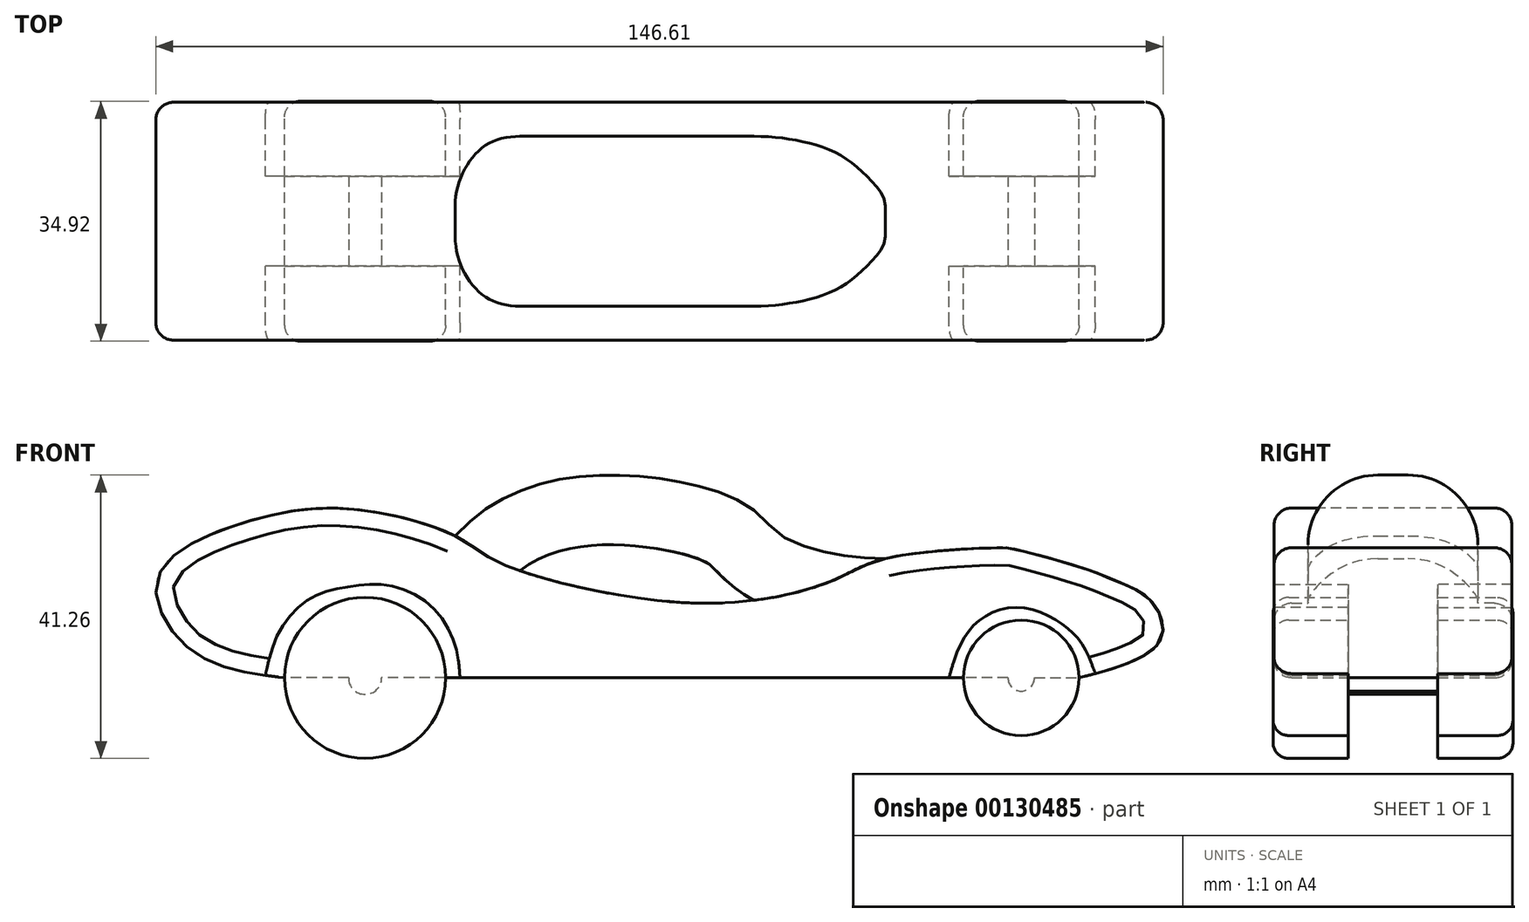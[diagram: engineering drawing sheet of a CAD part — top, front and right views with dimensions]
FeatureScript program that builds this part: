
annotation { "Feature Type Name" : "Feature", "Feature Type Description" : "" }
export const myFeature = defineFeature(function(context is Context, id is Id, definition is map)
    precondition{}
    {
        {
            var Q0;
            Q0=qCreatedBy(makeId("Front.planeOp"),FACE);
            var sketch = newSketch(context, id + "F0", { "sketchPlane" : qUnion([Q0])});
            skLineSegment(sketch, "E0", {"start": v(0, 0) * mm, "end": v(-51.5, 0) * mm});
            skLineSegment(sketch, "E1", {"start": v(0, 0) * mm, "end": v(34.83, 0) * mm});
            skCircle(sketch, "E2", {"center": v(-60.68, 0) * mm, "radius": 11.72 * mm});
            skCircle(sketch, "E3", {"center": v(34.83, 0) * mm, "radius": 8.41 * mm});
            skFitSpline(sketch, "E4", {"points": [v(-72.4, 0) * mm, v(-80.61, 1.45) * mm, v(-87.78, 5.65) * mm, v(-90.75, 14.91) * mm, v(-77.12, 22.96) * mm, v(-62.08, 24.53) * mm, v(-47.56, 20.68) * mm, v(-41.97, 17.19) * mm, v(-25, 12.29) * mm, v(-6.12, 11.07) * mm, v(7.52, 14.21) * mm, v(15.04, 17.36) * mm, v(31.47, 18.93) * mm, v(34.62, 18.59) * mm, v(45.46, 15.44) * mm, v(47.91, 14.39) * mm, v(53.5, 11.42) * mm, v(55.26, 5.82) * mm, v(50.36, 2.15) * mm, v(43.24, 0) * mm], "startDerivative": vector(-172.28, 21.35) * mm, "endDerivative": vector(-155.47, -39.98) * mm});
            skFitSpline(sketch, "E5", {"points": [v(-46.86, 0) * mm, v(-47.74, 5.3) * mm, v(-51.59, 10.9) * mm, v(-57.7, 13.51) * mm, v(-63.65, 13.16) * mm, v(-68.9, 11.42) * mm, v(-73.27, 6.52) * mm, v(-75.2, 0.35) * mm], "startDerivative": vector(-2.75, 39.39) * mm, "endDerivative": vector(-9.39, -43.26) * mm});
            skFitSpline(sketch, "E6", {"points": [v(24.3, 0) * mm, v(26.4, 5.65) * mm, v(29.9, 9.14) * mm, v(35.15, 10.2) * mm, v(40.4, 8.1) * mm, v(43.54, 5.12) * mm, v(45.62, 0.61) * mm], "startDerivative": vector(9.62, 33.45) * mm, "endDerivative": vector(11.2, -29.67) * mm});
            skFitSpline(sketch, "E7", {"points": [v(-47.56, 20.68) * mm, v(-42.14, 25.23) * mm, v(-31.3, 29.08) * mm, v(-15.91, 28.73) * mm, v(-4.72, 24.88) * mm, v(0, 20.68) * mm, v(8.57, 17.89) * mm, v(15.04, 17.36) * mm], "startDerivative": vector(38.88, 38.37) * mm, "endDerivative": vector(50.96, -1.8) * mm});
            skCircle(sketch, "E8", {"center": v(-60.68, 0) * mm, "radius": 2.4 * mm});
            skCircle(sketch, "E9", {"center": v(34.83, 0) * mm, "radius": 1.93 * mm});
            skCircle(sketch, "E10", {"center": v(-60.68, 0) * mm, "radius": 9.22 * mm});
            skCircle(sketch, "E11", {"center": v(34.83, 0) * mm, "radius": 6.25 * mm});
            skLineSegment(sketch, "E12", {"start": v(34.83, 0) * mm, "end": v(43.24, 0) * mm});
            skLineSegment(sketch, "E13", {"start": v(-51.5, 0) * mm, "end": v(-72.4, 0) * mm});
            skArc(sketch, "E14", {"start": v(-73.25, 0.1) * mm, "mid": v(-60.54, -12.95) * mm, "end": v(-47.72, 0) * mm});
            skArc(sketch, "E15", {"start": v(25.75, 0) * mm, "mid": v(34.96, -9.02) * mm, "end": v(43.99, 0.2) * mm});
            skSolve(sketch);
        }
        {
            var Q0;
            {var subQ6=sQuery(id+"F0.wireOp",EDGE,"E1");var subQ7=sQuery(id+"F0.wireOp",EDGE,"E0");var subQ8=makeQuery(id+"F0.imprint","INTERSECT",VERTEX,{"derivedFrom":[subQ7,subQ6]});Q0=makeQuery(id+"F0.imprint","IMPRINT",FACE,{"disambiguationData":[TD([[makeQuery(id+"F0.imprint","IMPRINT",EDGE,{"disambiguationData":[TD([[subQ8,-1.0]])],"derivedFrom":subQ7}),-1.0]])]});}
            extrude(context, id + "F1", {"entities" : qUnion([Q0]), "endBound" : BoundingType.SYMMETRIC, "depth" : 34.63 * mm});
        }
        {
            var Q0;
            {var subQ0=sQuery(id+"F0.wireOp",EDGE,"E7");Q0=makeQuery(id+"F0.imprint","IMPRINT",FACE,{"disambiguationData":[TD([[makeQuery(id+"F0.imprint","IMPRINT",EDGE,{"derivedFrom":subQ0}),-1.0]])]});}
            extrude(context, id + "F2", {"entities" : qUnion([Q0]), "operationType" : NewBodyOperationType.ADD, "endBound" : BoundingType.SYMMETRIC, "depth" : 24.74 * mm});
        }
        {
            var Q0;
            {var subQ0=sQuery(id+"F0.wireOp",EDGE,"E3");var subQ1=sQuery(id+"F0.wireOp",EDGE,"E1");var subQ2=makeQuery(id+"F0.imprint","INTERSECT",VERTEX,{"derivedFrom":[subQ1,subQ0]});Q0=makeQuery(id+"F0.imprint","IMPRINT",FACE,{"disambiguationData":[TD([[makeQuery(id+"F0.imprint","IMPRINT",EDGE,{"disambiguationData":[TD([[subQ2,-1.0]])],"derivedFrom":subQ1}),-1.0]])]});}
            var Q1;
            {var subQ0=sQuery(id+"F0.wireOp",EDGE,"E11");var subQ1=sQuery(id+"F0.wireOp",EDGE,"E1");var subQ2=makeQuery(id+"F0.imprint","INTERSECT",VERTEX,{"derivedFrom":[subQ1,subQ0]});Q1=makeQuery(id+"F0.imprint","IMPRINT",FACE,{"disambiguationData":[TD([[makeQuery(id+"F0.imprint","IMPRINT",EDGE,{"disambiguationData":[TD([[subQ2,-1.0]])],"derivedFrom":subQ1}),-1.0]])]});}
            var Q2;
            {var subQ0=sQuery(id+"F0.wireOp",EDGE,"E12");var subQ1=sQuery(id+"F0.wireOp",EDGE,"E1");var subQ2=makeQuery(id+"F0.imprint","INTERSECT",VERTEX,{"derivedFrom":[subQ1,subQ0]});Q2=makeQuery(id+"F0.imprint","IMPRINT",FACE,{"disambiguationData":[TD([[makeQuery(id+"F0.imprint","IMPRINT",EDGE,{"disambiguationData":[TD([[subQ2,1.0]])],"derivedFrom":subQ1}),-1.0]])]});}
            var Q3;
            {var subQ0=sQuery(id+"F0.wireOp",EDGE,"E11");var subQ1=sQuery(id+"F0.wireOp",EDGE,"E1");var subQ2=makeQuery(id+"F0.imprint","INTERSECT",VERTEX,{"derivedFrom":[subQ1,subQ0]});Q3=makeQuery(id+"F0.imprint","IMPRINT",FACE,{"disambiguationData":[TD([[makeQuery(id+"F0.imprint","IMPRINT",EDGE,{"disambiguationData":[TD([[subQ2,-1.0]])],"derivedFrom":subQ1}),1.0]])]});}
            var Q4;
            {var subQ0=sQuery(id+"F0.wireOp",EDGE,"E12");var subQ1=sQuery(id+"F0.wireOp",EDGE,"E1");var subQ2=makeQuery(id+"F0.imprint","INTERSECT",VERTEX,{"derivedFrom":[subQ1,subQ0]});Q4=makeQuery(id+"F0.imprint","IMPRINT",FACE,{"disambiguationData":[TD([[makeQuery(id+"F0.imprint","IMPRINT",EDGE,{"disambiguationData":[TD([[subQ2,1.0]])],"derivedFrom":subQ1}),1.0]])]});}
            var Q5;
            {var subQ0=sQuery(id+"F0.wireOp",EDGE,"E3");var subQ1=sQuery(id+"F0.wireOp",EDGE,"E1");var subQ2=makeQuery(id+"F0.imprint","INTERSECT",VERTEX,{"derivedFrom":[subQ1,subQ0]});Q5=makeQuery(id+"F0.imprint","IMPRINT",FACE,{"disambiguationData":[TD([[makeQuery(id+"F0.imprint","IMPRINT",EDGE,{"disambiguationData":[TD([[subQ2,-1.0]])],"derivedFrom":subQ1}),1.0]])]});}
            var Q6;
            {var subQ0=sQuery(id+"F0.wireOp",EDGE,"E2");var subQ1=sQuery(id+"F0.wireOp",EDGE,"E0");var subQ2=makeQuery(id+"F0.imprint","INTERSECT",VERTEX,{"derivedFrom":[subQ1,subQ0]});Q6=makeQuery(id+"F0.imprint","IMPRINT",FACE,{"disambiguationData":[TD([[makeQuery(id+"F0.imprint","IMPRINT",EDGE,{"disambiguationData":[TD([[subQ2,-1.0]])],"derivedFrom":subQ1}),-1.0]])]});}
            var Q7;
            {var subQ1=sQuery(id+"F0.wireOp",EDGE,"E0");var subQ3=sQuery(id+"F0.wireOp",EDGE,"E13");var subQ8=makeQuery(id+"F0.imprint","INTERSECT",VERTEX,{"derivedFrom":[subQ1,subQ3]});Q7=makeQuery(id+"F0.imprint","IMPRINT",FACE,{"disambiguationData":[TD([[makeQuery(id+"F0.imprint","IMPRINT",EDGE,{"disambiguationData":[TD([[subQ8,1.0]])],"derivedFrom":subQ1}),-1.0]])]});}
            var Q8;
            {var subQ1=sQuery(id+"F0.wireOp",EDGE,"E0");var subQ3=sQuery(id+"F0.wireOp",EDGE,"E13");var subQ8=makeQuery(id+"F0.imprint","INTERSECT",VERTEX,{"derivedFrom":[subQ1,subQ3]});Q8=makeQuery(id+"F0.imprint","IMPRINT",FACE,{"disambiguationData":[TD([[makeQuery(id+"F0.imprint","IMPRINT",EDGE,{"disambiguationData":[TD([[subQ8,1.0]])],"derivedFrom":subQ1}),1.0]])]});}
            var Q9;
            {var subQ0=sQuery(id+"F0.wireOp",EDGE,"E2");var subQ1=sQuery(id+"F0.wireOp",EDGE,"E0");var subQ2=makeQuery(id+"F0.imprint","INTERSECT",VERTEX,{"derivedFrom":[subQ1,subQ0]});Q9=makeQuery(id+"F0.imprint","IMPRINT",FACE,{"disambiguationData":[TD([[makeQuery(id+"F0.imprint","IMPRINT",EDGE,{"disambiguationData":[TD([[subQ2,-1.0]])],"derivedFrom":subQ1}),1.0]])]});}
            var Q10;
            {var subQ0=sQuery(id+"F0.wireOp",EDGE,"E13");var subQ1=sQuery(id+"F0.wireOp",EDGE,"E8");var subQ2=makeQuery(id+"F0.imprint","INTERSECT",VERTEX,{"disambiguationData":[OD(0.0)],"derivedFrom":[subQ1,subQ0]});Q10=makeQuery(id+"F0.imprint","IMPRINT",FACE,{"disambiguationData":[TD([[makeQuery(id+"F0.imprint","IMPRINT",EDGE,{"disambiguationData":[TD([[subQ2,1.0]])],"derivedFrom":subQ1}),1.0]])]});}
            var Q11;
            {var subQ0=sQuery(id+"F0.wireOp",EDGE,"E13");var subQ1=sQuery(id+"F0.wireOp",EDGE,"E8");var subQ2=makeQuery(id+"F0.imprint","INTERSECT",VERTEX,{"disambiguationData":[OD(0.0)],"derivedFrom":[subQ1,subQ0]});Q11=makeQuery(id+"F0.imprint","IMPRINT",FACE,{"disambiguationData":[TD([[makeQuery(id+"F0.imprint","IMPRINT",EDGE,{"disambiguationData":[TD([[subQ2,-1.0]])],"derivedFrom":subQ1}),1.0]])]});}
            extrude(context, id + "F3", {"entities" : qUnion([Q0, Q1, Q2, Q3, Q4, Q5, Q6, Q7, Q8, Q9, Q10, Q11]), "endBound" : BoundingType.SYMMETRIC, "depth" : 34.92 * mm});
        }
        {
            var Q0;
            {var subQ0=sQuery(id+"F0.wireOp",EDGE,"E5");var subQ1=sQuery(id+"F0.wireOp",EDGE,"E0");var subQ2=makeQuery(id+"F0.imprint","INTERSECT",VERTEX,{"derivedFrom":[subQ1,subQ0]});Q0=makeQuery(id+"F0.imprint","IMPRINT",FACE,{"disambiguationData":[TD([[makeQuery(id+"F0.imprint","IMPRINT",EDGE,{"disambiguationData":[TD([[subQ2,-1.0]])],"derivedFrom":subQ1}),-1.0]])]});}
            var Q1;
            {var subQ1=sQuery(id+"F0.wireOp",EDGE,"E0");var subQ3=sQuery(id+"F0.wireOp",EDGE,"E13");var subQ8=makeQuery(id+"F0.imprint","INTERSECT",VERTEX,{"derivedFrom":[subQ1,subQ3]});Q1=makeQuery(id+"F0.imprint","IMPRINT",FACE,{"disambiguationData":[TD([[makeQuery(id+"F0.imprint","IMPRINT",EDGE,{"disambiguationData":[TD([[subQ8,1.0]])],"derivedFrom":subQ1}),-1.0]])]});}
            var Q2;
            {var subQ0=sQuery(id+"F0.wireOp",EDGE,"E2");var subQ1=sQuery(id+"F0.wireOp",EDGE,"E0");var subQ2=makeQuery(id+"F0.imprint","INTERSECT",VERTEX,{"derivedFrom":[subQ1,subQ0]});Q2=makeQuery(id+"F0.imprint","IMPRINT",FACE,{"disambiguationData":[TD([[makeQuery(id+"F0.imprint","IMPRINT",EDGE,{"disambiguationData":[TD([[subQ2,-1.0]])],"derivedFrom":subQ1}),-1.0]])]});}
            var Q3;
            {var subQ0=sQuery(id+"F0.wireOp",EDGE,"E13");var subQ1=sQuery(id+"F0.wireOp",EDGE,"E8");var subQ2=makeQuery(id+"F0.imprint","INTERSECT",VERTEX,{"disambiguationData":[OD(0.0)],"derivedFrom":[subQ1,subQ0]});Q3=makeQuery(id+"F0.imprint","IMPRINT",FACE,{"disambiguationData":[TD([[makeQuery(id+"F0.imprint","IMPRINT",EDGE,{"disambiguationData":[TD([[subQ2,-1.0]])],"derivedFrom":subQ1}),1.0]])]});}
            var Q4;
            {var subQ0=sQuery(id+"F0.wireOp",EDGE,"E3");var subQ1=sQuery(id+"F0.wireOp",EDGE,"E1");var subQ2=makeQuery(id+"F0.imprint","INTERSECT",VERTEX,{"derivedFrom":[subQ1,subQ0]});Q4=makeQuery(id+"F0.imprint","IMPRINT",FACE,{"disambiguationData":[TD([[makeQuery(id+"F0.imprint","IMPRINT",EDGE,{"disambiguationData":[TD([[subQ2,-1.0]])],"derivedFrom":subQ1}),1.0]])]});}
            var Q5;
            {var subQ0=sQuery(id+"F0.wireOp",EDGE,"E6");var subQ1=sQuery(id+"F0.wireOp",EDGE,"E1");var subQ2=makeQuery(id+"F0.imprint","INTERSECT",VERTEX,{"derivedFrom":[subQ1,subQ0]});Q5=makeQuery(id+"F0.imprint","IMPRINT",FACE,{"disambiguationData":[TD([[makeQuery(id+"F0.imprint","IMPRINT",EDGE,{"disambiguationData":[TD([[subQ2,-1.0]])],"derivedFrom":subQ1}),1.0]])]});}
            var Q6;
            {var subQ0=sQuery(id+"F0.wireOp",EDGE,"E11");var subQ1=sQuery(id+"F0.wireOp",EDGE,"E1");var subQ2=makeQuery(id+"F0.imprint","INTERSECT",VERTEX,{"derivedFrom":[subQ1,subQ0]});Q6=makeQuery(id+"F0.imprint","IMPRINT",FACE,{"disambiguationData":[TD([[makeQuery(id+"F0.imprint","IMPRINT",EDGE,{"disambiguationData":[TD([[subQ2,-1.0]])],"derivedFrom":subQ1}),1.0]])]});}
            var Q7;
            {var subQ0=sQuery(id+"F0.wireOp",EDGE,"E12");var subQ1=sQuery(id+"F0.wireOp",EDGE,"E1");var subQ2=makeQuery(id+"F0.imprint","INTERSECT",VERTEX,{"derivedFrom":[subQ1,subQ0]});Q7=makeQuery(id+"F0.imprint","IMPRINT",FACE,{"disambiguationData":[TD([[makeQuery(id+"F0.imprint","IMPRINT",EDGE,{"disambiguationData":[TD([[subQ2,1.0]])],"derivedFrom":subQ1}),1.0]])]});}
            extrude(context, id + "F4", {"entities" : qUnion([Q0, Q1, Q2, Q3, Q4, Q5, Q6, Q7]), "operationType" : NewBodyOperationType.ADD, "endBound" : BoundingType.SYMMETRIC, "depth" : 13.04 * mm});
        }
        {
            var Q0;
            Q0=makeQuery(id+"F2.opExtrude","CAP_EDGE",EDGE,{"disambiguationData":[OSD([sQuery(id+"F0.wireOp",EDGE,"E7")])],"isStart":true});
            var Q1;
            Q1=makeQuery(id+"F2.opExtrude","CAP_EDGE",EDGE,{"disambiguationData":[OSD([sQuery(id+"F0.wireOp",EDGE,"E7")])],"isStart":false});
            fillet(context, id + "F5", {"entities" : qUnion([Q0, Q1]), "radius" : 10.16 * mm, "tangentPropagation" : true, "allowEdgeOverflow" : false});
        }
        {
            var Q0;
            Q0=makeQuery(id+"F1.opExtrude","CAP_EDGE",EDGE,{"disambiguationData":[OSD([sQuery(id+"F0.wireOp",EDGE,"E0"),sQuery(id+"F0.wireOp",EDGE,"E1")])],"isStart":false});
            var Q1;
            Q1=makeQuery(id+"F1.opExtrude","CAP_EDGE",EDGE,{"disambiguationData":[OSD([sQuery(id+"F0.wireOp",EDGE,"E0"),sQuery(id+"F0.wireOp",EDGE,"E1")])],"isStart":true});
            fillet(context, id + "F6", {"entities" : qUnion([Q0, Q1]), "radius" : 2.54 * mm, "tangentPropagation" : true, "allowEdgeOverflow" : false});
        }
        {
            var Q0;
            Q0=makeQuery(id+"F1.opExtrude","CAP_EDGE",EDGE,{"disambiguationData":[OSD([sQuery(id+"F0.wireOp",EDGE,"E4")])],"isStart":false});
            var Q1;
            Q1=makeQuery(id+"F1.opExtrude","CAP_EDGE",EDGE,{"disambiguationData":[OSD([sQuery(id+"F0.wireOp",EDGE,"E4")])],"isStart":true});
            fillet(context, id + "F7", {"entities" : qUnion([Q0, Q1]), "radius" : 2.54 * mm, "tangentPropagation" : true, "allowEdgeOverflow" : false});
        }
        {
            var Q0;
            Q0=makeQuery(id+"F3.opExtrude","CAP_EDGE",EDGE,{"disambiguationData":[OSD([sQuery(id+"F0.wireOp",EDGE,"E2")])],"isStart":false});
            var Q1;
            Q1=makeQuery(id+"F3.opExtrude","CAP_EDGE",EDGE,{"disambiguationData":[OSD([sQuery(id+"F0.wireOp",EDGE,"E3")])],"isStart":false});
            fillet(context, id + "F8", {"entities" : qUnion([Q0, Q1]), "radius" : 2.3 * mm, "tangentPropagation" : true, "allowEdgeOverflow" : false});
        }
        {
            var Q0;
            Q0=makeQuery(id+"F3.opExtrude","CAP_EDGE",EDGE,{"disambiguationData":[OSD([sQuery(id+"F0.wireOp",EDGE,"E3")])],"isStart":true});
            var Q1;
            Q1=makeQuery(id+"F3.opExtrude","CAP_EDGE",EDGE,{"disambiguationData":[OSD([sQuery(id+"F0.wireOp",EDGE,"E2")])],"isStart":true});
            fillet(context, id + "F9", {"entities" : qUnion([Q0, Q1]), "radius" : 2.3 * mm, "tangentPropagation" : true, "allowEdgeOverflow" : false});
        }
        {
            var Q0;
            {var subQ0=sQuery(id+"F0.wireOp",EDGE,"E15");Q0=makeQuery(id+"F0.imprint","IMPRINT",FACE,{"disambiguationData":[TD([[makeQuery(id+"F0.imprint","IMPRINT",EDGE,{"derivedFrom":subQ0}),1.0]])]});}
            var Q1;
            {var subQ0=sQuery(id+"F0.wireOp",EDGE,"E3");var subQ1=sQuery(id+"F0.wireOp",EDGE,"E1");var subQ2=makeQuery(id+"F0.imprint","INTERSECT",VERTEX,{"derivedFrom":[subQ1,subQ0]});Q1=makeQuery(id+"F0.imprint","IMPRINT",FACE,{"disambiguationData":[TD([[makeQuery(id+"F0.imprint","IMPRINT",EDGE,{"disambiguationData":[TD([[subQ2,-1.0]])],"derivedFrom":subQ1}),-1.0]])]});}
            var Q2;
            {var subQ0=sQuery(id+"F0.wireOp",EDGE,"E11");var subQ1=sQuery(id+"F0.wireOp",EDGE,"E1");var subQ2=makeQuery(id+"F0.imprint","INTERSECT",VERTEX,{"derivedFrom":[subQ1,subQ0]});Q2=makeQuery(id+"F0.imprint","IMPRINT",FACE,{"disambiguationData":[TD([[makeQuery(id+"F0.imprint","IMPRINT",EDGE,{"disambiguationData":[TD([[subQ2,-1.0]])],"derivedFrom":subQ1}),-1.0]])]});}
            var Q3;
            {var subQ1=sQuery(id+"F0.wireOp",EDGE,"E0");var subQ3=sQuery(id+"F0.wireOp",EDGE,"E13");var subQ8=makeQuery(id+"F0.imprint","INTERSECT",VERTEX,{"derivedFrom":[subQ1,subQ3]});Q3=makeQuery(id+"F0.imprint","IMPRINT",FACE,{"disambiguationData":[TD([[makeQuery(id+"F0.imprint","IMPRINT",EDGE,{"disambiguationData":[TD([[subQ8,1.0]])],"derivedFrom":subQ1}),1.0]])]});}
            var Q4;
            {var subQ0=sQuery(id+"F0.wireOp",EDGE,"E2");var subQ1=sQuery(id+"F0.wireOp",EDGE,"E0");var subQ2=makeQuery(id+"F0.imprint","INTERSECT",VERTEX,{"derivedFrom":[subQ1,subQ0]});Q4=makeQuery(id+"F0.imprint","IMPRINT",FACE,{"disambiguationData":[TD([[makeQuery(id+"F0.imprint","IMPRINT",EDGE,{"disambiguationData":[TD([[subQ2,-1.0]])],"derivedFrom":subQ1}),1.0]])]});}
            var Q5;
            {var subQ0=sQuery(id+"F0.wireOp",EDGE,"E14");Q5=makeQuery(id+"F0.imprint","IMPRINT",FACE,{"disambiguationData":[TD([[makeQuery(id+"F0.imprint","IMPRINT",EDGE,{"derivedFrom":subQ0}),1.0]])]});}
            extrude(context, id + "F10", {"entities" : qUnion([Q0, Q1, Q2, Q3, Q4, Q5]), "operationType" : NewBodyOperationType.REMOVE, "endBound" : BoundingType.SYMMETRIC, "oppositeDirection" : true, "depth" : 13.04 * mm});
        }
    });
